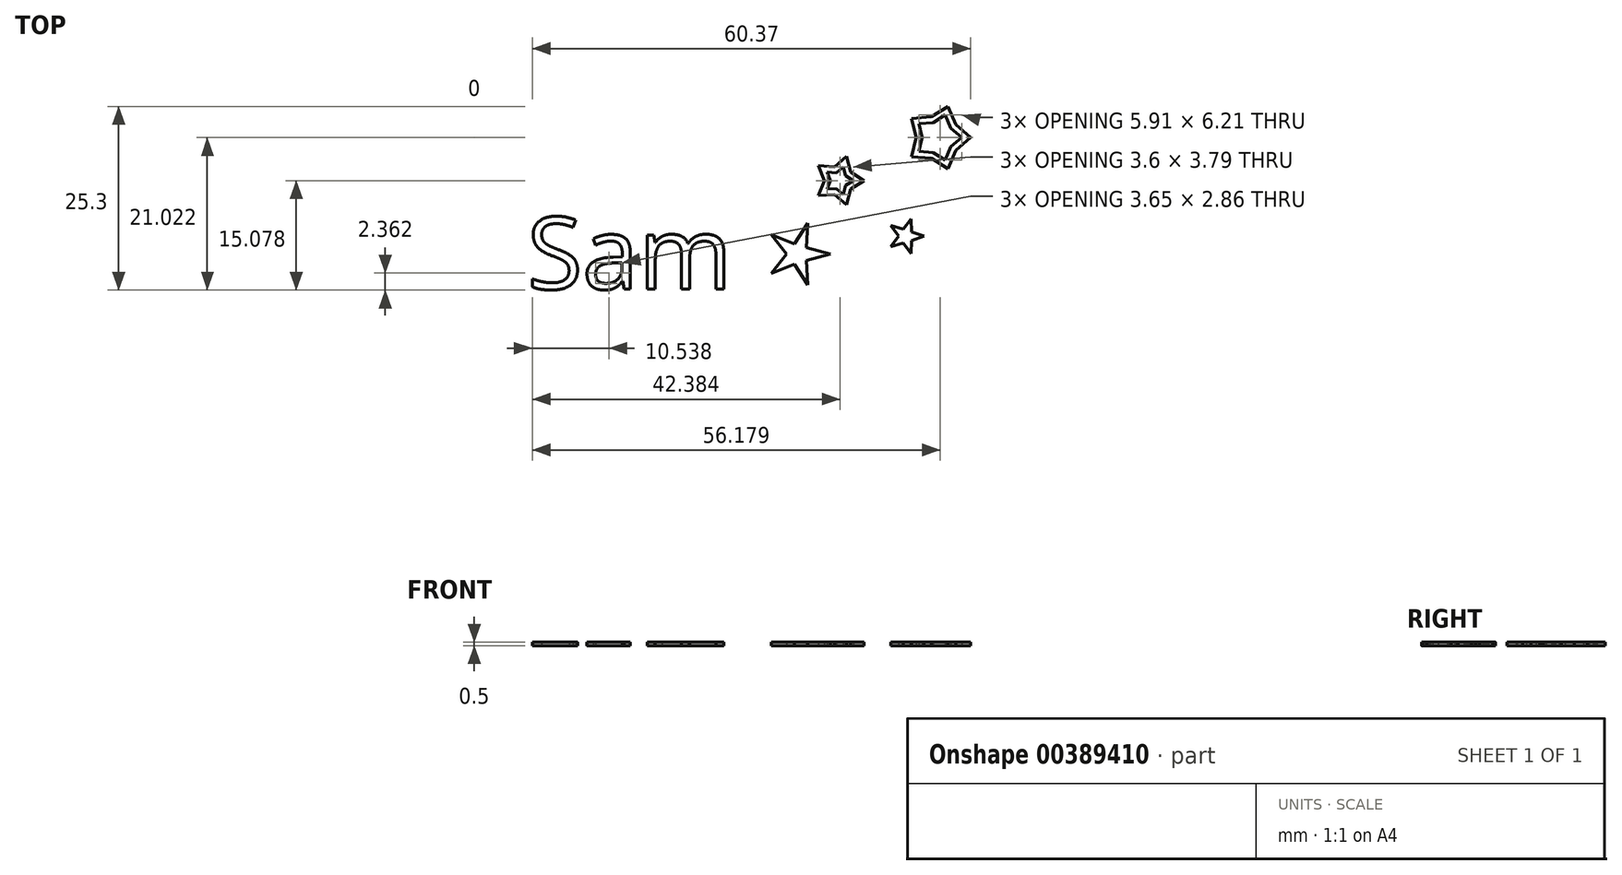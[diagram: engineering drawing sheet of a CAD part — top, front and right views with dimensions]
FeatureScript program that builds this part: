
annotation { "Feature Type Name" : "Feature", "Feature Type Description" : "" }
export const myFeature = defineFeature(function(context is Context, id is Id, definition is map)
    precondition{}
    {
        {
            var Q0;
            Q0=qCreatedBy(makeId("Top.planeOp"),FACE);
            var sketch = newSketch(context, id + "F0", { "sketchPlane" : qUnion([Q0])});
            skCircle(sketch, "E0.cCircle", {"center": v(46.45, 16.36) * mm, "radius": 4.5 * mm, "construction": true});
            skLineSegment(sketch, "E0.0", {"start": v(50.95, 16.36) * mm, "end": v(47.84, 12.08) * mm, "construction": true});
            skLineSegment(sketch, "E0.1", {"start": v(47.84, 12.08) * mm, "end": v(42.8, 13.72) * mm, "construction": true});
            skLineSegment(sketch, "E0.2", {"start": v(42.8, 13.72) * mm, "end": v(42.8, 19) * mm, "construction": true});
            skLineSegment(sketch, "E0.3", {"start": v(42.8, 19) * mm, "end": v(47.84, 20.64) * mm, "construction": true});
            skLineSegment(sketch, "E0.4", {"start": v(47.84, 20.64) * mm, "end": v(50.95, 16.36) * mm, "construction": true});
            skCircle(sketch, "E1.cCircle", {"center": v(46.45, 16.36) * mm, "radius": 3 * mm, "construction": true});
            skLineSegment(sketch, "E1.0", {"start": v(48.87, 18.13) * mm, "end": v(48.87, 14.6) * mm, "construction": true});
            skLineSegment(sketch, "E1.1", {"start": v(48.87, 14.6) * mm, "end": v(45.52, 13.5) * mm, "construction": true});
            skLineSegment(sketch, "E1.2", {"start": v(45.52, 13.5) * mm, "end": v(43.45, 16.36) * mm, "construction": true});
            skLineSegment(sketch, "E1.3", {"start": v(43.45, 16.36) * mm, "end": v(45.52, 19.21) * mm, "construction": true});
            skLineSegment(sketch, "E1.4", {"start": v(45.52, 19.21) * mm, "end": v(48.87, 18.13) * mm, "construction": true});
            skLineSegment(sketch, "E2", {"start": v(42.8, 19) * mm, "end": v(43.45, 16.36) * mm});
            skLineSegment(sketch, "E3", {"start": v(42.8, 13.72) * mm, "end": v(43.45, 16.36) * mm});
            skLineSegment(sketch, "E4", {"start": v(42.8, 13.72) * mm, "end": v(45.52, 13.5) * mm});
            skLineSegment(sketch, "E5", {"start": v(45.52, 13.5) * mm, "end": v(47.84, 12.08) * mm});
            skLineSegment(sketch, "E6", {"start": v(47.84, 12.08) * mm, "end": v(48.87, 14.6) * mm});
            skLineSegment(sketch, "E7", {"start": v(48.87, 14.6) * mm, "end": v(50.95, 16.36) * mm});
            skLineSegment(sketch, "E8", {"start": v(50.95, 16.36) * mm, "end": v(48.87, 18.13) * mm});
            skLineSegment(sketch, "E9", {"start": v(48.87, 18.13) * mm, "end": v(47.84, 20.64) * mm});
            skLineSegment(sketch, "E10", {"start": v(47.84, 20.64) * mm, "end": v(45.52, 19.21) * mm});
            skLineSegment(sketch, "E11", {"start": v(45.52, 19.21) * mm, "end": v(42.8, 19) * mm});
            skCircle(sketch, "E12.cCircle", {"center": v(32.77, 10.42) * mm, "radius": 3.5 * mm, "construction": true});
            skLineSegment(sketch, "E12.0", {"start": v(36.27, 10.42) * mm, "end": v(33.86, 7.09) * mm, "construction": true});
            skLineSegment(sketch, "E12.1", {"start": v(33.86, 7.09) * mm, "end": v(29.94, 8.36) * mm, "construction": true});
            skLineSegment(sketch, "E12.2", {"start": v(29.94, 8.36) * mm, "end": v(29.94, 12.47) * mm, "construction": true});
            skLineSegment(sketch, "E12.3", {"start": v(29.94, 12.47) * mm, "end": v(33.86, 13.75) * mm, "construction": true});
            skLineSegment(sketch, "E12.4", {"start": v(33.86, 13.75) * mm, "end": v(36.27, 10.42) * mm, "construction": true});
            skCircle(sketch, "E13.cCircle", {"center": v(32.77, 10.42) * mm, "radius": 2 * mm, "construction": true});
            skLineSegment(sketch, "E13.0", {"start": v(34.4, 11.6) * mm, "end": v(34.4, 9.24) * mm, "construction": true});
            skLineSegment(sketch, "E13.1", {"start": v(34.4, 9.24) * mm, "end": v(32.16, 8.52) * mm, "construction": true});
            skLineSegment(sketch, "E13.2", {"start": v(32.16, 8.52) * mm, "end": v(30.77, 10.42) * mm, "construction": true});
            skLineSegment(sketch, "E13.3", {"start": v(30.77, 10.42) * mm, "end": v(32.16, 12.32) * mm, "construction": true});
            skLineSegment(sketch, "E13.4", {"start": v(32.16, 12.32) * mm, "end": v(34.4, 11.6) * mm, "construction": true});
            skLineSegment(sketch, "E14", {"start": v(29.94, 12.47) * mm, "end": v(30.77, 10.42) * mm});
            skLineSegment(sketch, "E15", {"start": v(29.94, 8.36) * mm, "end": v(30.77, 10.42) * mm});
            skLineSegment(sketch, "E16", {"start": v(29.94, 8.36) * mm, "end": v(32.16, 8.52) * mm});
            skLineSegment(sketch, "E17", {"start": v(32.16, 8.52) * mm, "end": v(33.86, 7.09) * mm});
            skLineSegment(sketch, "E18", {"start": v(33.86, 7.09) * mm, "end": v(34.4, 9.24) * mm});
            skLineSegment(sketch, "E19", {"start": v(34.4, 9.24) * mm, "end": v(36.27, 10.42) * mm});
            skLineSegment(sketch, "E20", {"start": v(36.27, 10.42) * mm, "end": v(34.4, 11.6) * mm});
            skLineSegment(sketch, "E21", {"start": v(34.4, 11.6) * mm, "end": v(33.86, 13.75) * mm});
            skLineSegment(sketch, "E22", {"start": v(33.86, 13.75) * mm, "end": v(32.16, 12.32) * mm});
            skLineSegment(sketch, "E23", {"start": v(32.16, 12.32) * mm, "end": v(29.94, 12.47) * mm});
            skCircle(sketch, "E24.cCircle", {"center": v(41.99, 2.77) * mm, "radius": 2.5 * mm, "construction": true});
            skLineSegment(sketch, "E24.0", {"start": v(44.49, 2.77) * mm, "end": v(42.76, 0.39) * mm, "construction": true});
            skLineSegment(sketch, "E24.1", {"start": v(42.76, 0.39) * mm, "end": v(39.97, 1.3) * mm, "construction": true});
            skLineSegment(sketch, "E24.2", {"start": v(39.97, 1.3) * mm, "end": v(39.97, 4.24) * mm, "construction": true});
            skLineSegment(sketch, "E24.3", {"start": v(39.97, 4.24) * mm, "end": v(42.76, 5.14) * mm, "construction": true});
            skLineSegment(sketch, "E24.4", {"start": v(42.76, 5.14) * mm, "end": v(44.49, 2.77) * mm, "construction": true});
            skCircle(sketch, "E25.cCircle", {"center": v(41.99, 2.77) * mm, "radius": 1 * mm, "construction": true});
            skLineSegment(sketch, "E25.0", {"start": v(42.8, 3.36) * mm, "end": v(42.8, 2.18) * mm, "construction": true});
            skLineSegment(sketch, "E25.1", {"start": v(42.8, 2.18) * mm, "end": v(41.68, 1.82) * mm, "construction": true});
            skLineSegment(sketch, "E25.2", {"start": v(41.68, 1.82) * mm, "end": v(40.99, 2.77) * mm, "construction": true});
            skLineSegment(sketch, "E25.3", {"start": v(40.99, 2.77) * mm, "end": v(41.68, 3.72) * mm, "construction": true});
            skLineSegment(sketch, "E25.4", {"start": v(41.68, 3.72) * mm, "end": v(42.8, 3.36) * mm, "construction": true});
            skLineSegment(sketch, "E26", {"start": v(39.97, 4.24) * mm, "end": v(40.99, 2.77) * mm});
            skLineSegment(sketch, "E27", {"start": v(39.97, 1.3) * mm, "end": v(40.99, 2.77) * mm});
            skLineSegment(sketch, "E28", {"start": v(39.97, 1.3) * mm, "end": v(41.68, 1.82) * mm});
            skLineSegment(sketch, "E29", {"start": v(41.68, 1.82) * mm, "end": v(42.76, 0.39) * mm});
            skLineSegment(sketch, "E30", {"start": v(42.76, 0.39) * mm, "end": v(42.8, 2.18) * mm});
            skLineSegment(sketch, "E31", {"start": v(42.8, 2.18) * mm, "end": v(44.49, 2.77) * mm});
            skLineSegment(sketch, "E32", {"start": v(44.49, 2.77) * mm, "end": v(42.8, 3.36) * mm});
            skLineSegment(sketch, "E33", {"start": v(42.8, 3.36) * mm, "end": v(42.76, 5.14) * mm});
            skLineSegment(sketch, "E34", {"start": v(42.76, 5.14) * mm, "end": v(41.68, 3.72) * mm});
            skLineSegment(sketch, "E35", {"start": v(41.68, 3.72) * mm, "end": v(39.97, 4.24) * mm});
            skCircle(sketch, "E36.cCircle", {"center": v(27.11, 0.31) * mm, "radius": 4.5 * mm, "construction": true});
            skLineSegment(sketch, "E36.0", {"start": v(31.61, 0.31) * mm, "end": v(28.5, -3.97) * mm, "construction": true});
            skLineSegment(sketch, "E36.1", {"start": v(28.5, -3.97) * mm, "end": v(23.47, -2.33) * mm, "construction": true});
            skLineSegment(sketch, "E36.2", {"start": v(23.47, -2.33) * mm, "end": v(23.47, 2.96) * mm, "construction": true});
            skLineSegment(sketch, "E36.3", {"start": v(23.47, 2.96) * mm, "end": v(28.5, 4.6) * mm, "construction": true});
            skLineSegment(sketch, "E36.4", {"start": v(28.5, 4.6) * mm, "end": v(31.61, 0.31) * mm, "construction": true});
            skCircle(sketch, "E37.cCircle", {"center": v(27.11, 0.31) * mm, "radius": 1.5 * mm, "construction": true});
            skLineSegment(sketch, "E37.0", {"start": v(28.32, 1.2) * mm, "end": v(28.32, -0.57) * mm, "construction": true});
            skLineSegment(sketch, "E37.1", {"start": v(28.32, -0.57) * mm, "end": v(26.65, -1.11) * mm, "construction": true});
            skLineSegment(sketch, "E37.2", {"start": v(26.65, -1.11) * mm, "end": v(25.61, 0.31) * mm, "construction": true});
            skLineSegment(sketch, "E37.3", {"start": v(25.61, 0.31) * mm, "end": v(26.65, 1.74) * mm, "construction": true});
            skLineSegment(sketch, "E37.4", {"start": v(26.65, 1.74) * mm, "end": v(28.32, 1.2) * mm, "construction": true});
            skLineSegment(sketch, "E38", {"start": v(23.47, 2.96) * mm, "end": v(25.61, 0.31) * mm});
            skLineSegment(sketch, "E39", {"start": v(23.47, -2.33) * mm, "end": v(25.61, 0.31) * mm});
            skLineSegment(sketch, "E40", {"start": v(23.47, -2.33) * mm, "end": v(26.65, -1.11) * mm});
            skLineSegment(sketch, "E41", {"start": v(26.65, -1.11) * mm, "end": v(28.5, -3.97) * mm});
            skLineSegment(sketch, "E42", {"start": v(28.5, -3.97) * mm, "end": v(28.32, -0.57) * mm});
            skLineSegment(sketch, "E43", {"start": v(28.32, -0.57) * mm, "end": v(31.61, 0.31) * mm});
            skLineSegment(sketch, "E44", {"start": v(31.61, 0.31) * mm, "end": v(28.32, 1.2) * mm});
            skLineSegment(sketch, "E45", {"start": v(28.32, 1.2) * mm, "end": v(28.5, 4.6) * mm});
            skLineSegment(sketch, "E46", {"start": v(28.5, 4.6) * mm, "end": v(26.65, 1.74) * mm});
            skLineSegment(sketch, "E47", {"start": v(26.65, 1.74) * mm, "end": v(23.47, 2.96) * mm});
            skLineSegment(sketch, "E48.0", {"start": v(48.2, 17.64) * mm, "end": v(47.46, 19.47) * mm});
            skLineSegment(sketch, "E48.1", {"start": v(49.71, 16.36) * mm, "end": v(48.2, 17.64) * mm});
            skLineSegment(sketch, "E48.2", {"start": v(47.46, 19.47) * mm, "end": v(45.77, 18.43) * mm});
            skLineSegment(sketch, "E48.3", {"start": v(48.2, 15.08) * mm, "end": v(49.71, 16.36) * mm});
            skLineSegment(sketch, "E48.4", {"start": v(47.46, 13.26) * mm, "end": v(48.2, 15.08) * mm});
            skLineSegment(sketch, "E48.5", {"start": v(45.77, 14.3) * mm, "end": v(47.46, 13.26) * mm});
            skLineSegment(sketch, "E48.6", {"start": v(45.77, 18.43) * mm, "end": v(43.8, 18.28) * mm});
            skLineSegment(sketch, "E48.7", {"start": v(43.8, 18.28) * mm, "end": v(44.27, 16.36) * mm});
            skLineSegment(sketch, "E48.8", {"start": v(43.8, 14.44) * mm, "end": v(44.27, 16.36) * mm});
            skLineSegment(sketch, "E48.9", {"start": v(43.8, 14.44) * mm, "end": v(45.77, 14.3) * mm});
            skLineSegment(sketch, "E49.0", {"start": v(33.7, 11.09) * mm, "end": v(33.39, 12.31) * mm});
            skLineSegment(sketch, "E49.1", {"start": v(34.76, 10.42) * mm, "end": v(33.7, 11.09) * mm});
            skLineSegment(sketch, "E49.2", {"start": v(33.39, 12.31) * mm, "end": v(32.42, 11.5) * mm});
            skLineSegment(sketch, "E49.3", {"start": v(33.7, 9.75) * mm, "end": v(34.76, 10.42) * mm});
            skLineSegment(sketch, "E49.4", {"start": v(33.39, 8.53) * mm, "end": v(33.7, 9.75) * mm});
            skLineSegment(sketch, "E49.5", {"start": v(32.42, 9.34) * mm, "end": v(33.39, 8.53) * mm});
            skLineSegment(sketch, "E49.6", {"start": v(32.42, 11.5) * mm, "end": v(31.16, 11.59) * mm});
            skLineSegment(sketch, "E49.7", {"start": v(31.16, 11.59) * mm, "end": v(31.64, 10.42) * mm});
            skLineSegment(sketch, "E49.8", {"start": v(31.16, 9.25) * mm, "end": v(31.64, 10.42) * mm});
            skLineSegment(sketch, "E49.9", {"start": v(31.16, 9.25) * mm, "end": v(32.42, 9.34) * mm});
            skText(sketch, "E50", { "text": "Sam", "fontName": "OpenSans-Regular.ttf"});
            const initialGuessF0  = {"E50": [-0.01014, -0.00452, 1, 0, 0.00999]};
            skSetInitialGuess(sketch, initialGuessF0);
            skSolve(sketch);
        }
        {
            var Q0;
            Q0 = qSketchRegion(id + "F0", true);
            extrude(context, id + "F1", {"entities" : qUnion([Q0]), "depth" : 0.5 * mm});
        }
    });
